# Revit family: Hager-VOLTA-Hollow_wall-IP30-With_Cover-Without_DIN-Hosted-DE-de
name_source: partatom
category: Electrical Equipment
units: mm (PartAtom-declared; Revit-internal decimal feet)

## family parameters
Cut with Voids When Loaded = No
Host = Face
Maintain Annotation Orientation = Yes
Panel Configuration = Two Columns, Circuits Across
Part Type = Panelboard
Room Calculation Point = No
Round Connector Dimension = Use Diameter
Shared = No

## types (6) — shared parameters
BC_MODEL_ID = 1547175
BC_OBJECT_ID = 513479
BC_OBJECT_VERSION = #3
Code hager = ADD-EC000214_EU
EF000003 - Montageart = Hohlwand
EF000007 - Farbe = weiß
EF000008 - Breite = 348 mm  [stored 1.14173 ft]
EF000024 - UV-beständig = No
EF000049 - Tiefe = 98 mm  [stored 0.321522 ft]
EF000116 - RAL-Nummer = 9010
EF000118 - Mit Montageplatte = Yes
EF000218 - Einbautiefe = 89 mm  [stored 0.291995 ft]
EF000846 - Einbaubreite = 315 mm
EF001062 - EMV-Ausführung = No
EF001088 - Anbaumöglichkeit = Yes
EF001134 - DIN-Schiene = No
EF002950 - Breite in Teilungseinheiten = 12
EF004462 - Art der Schließung = sonstige
EF005474 - Schutzart (IP) = IP30
EF006244 - Transparenter Deckel/Tür = No
EF006306 - Mit Schloss = No
EF009212 - Ausführung Deckel = mit Ausschnitt
EF015776 - Erdungsklemmenblock = No
EF015777 - Neutralleiterklemmenblock = No
ETIM class code = EC000214
ETIM class name = Small distribution board
HG000002-Mit tür = Yes
HG000003-Bereich = VOLTA
HG000005-Dicke = 2 mm  [stored 0.00656168 ft]
HG000006-Flush mounted = Yes
HG000009-Doppelflügeligen Tür = No
HG000010-Asymmetrische Türen = No
HG000011-Leere Reihen von unten = No
HG000012-Türschwenkwinkel = 90.00°
HG000013-Tür links = No
HG000014-Tür rechts = Yes
HG000015-Sichtbarkeit der Türöffnung = Yes
HG000016-3D-Türsichtbarkeit = Yes
HG000017-Distanz zwischen den Polen = 18 mm  [stored 0.0590551 ft]
HG000060-RAL-number = 9010
HG000099-Onfly Template ID-de-DE = 507532
HGEF0002950-Breite in Teilungseinheiten = 12
Manufacturer = Hager
Name = VOLTA-Hollow_wall-IP30-With_Cover-Without_DIN-DE
Name BIM&CO = Electricity
Name hager = ADD_Enclosures_EC000214
Uniformat = Low Tension Service & Dist.
Uniformat code = D501001
zero-valued in all types: Default Elevation, EF000266 - Anzahl der Reihen, EF001131 - Innentiefe, HG000001-Anzahl der Spalten, HG000007-Anzahl der leeren Spalten, HG000008-Anzahl der leeren Reihen, HGEF000266-Anzahl der Reihen

## per-type parameters (varying)
| type | BC_VARIANT_ID | EF000040 - Höhe | EF000332 - Einbauhöhe | EF015941 - Signaldurchlassende Tür | HG000004-Herstellerreferenz |
| VOLTA-Hollow_wall_W348_H630_D98_12_Modular_Spacing-VH36NW | 1174185 | 630 mm  [stored 2.06693 ft] | 595 mm  [stored 1.9521 ft] | No | VH36NW |
| VOLTA-Hollow_wall_W348_H630_D98_12_Modular_Spacing-VH36WWH | 1174186 | 630 mm  [stored 2.06693 ft] | 595 mm  [stored 1.9521 ft] | Yes | VH36WWH |
| VOLTA-Hollow_wall_W348_H755_D98_12_Modular_Spacing-VH48NW | 1174187 | 755 mm  [stored 2.47703 ft] | 720 mm  [stored 2.3622 ft] | No | VH48NW |
| VOLTA-Hollow_wall_W348_H755_D98_12_Modular_Spacing-VH48WWH | 1174188 | 755 mm  [stored 2.47703 ft] | 720 mm  [stored 2.3622 ft] | Yes | VH48WWH |
| VOLTA-Hollow_wall_W348_H880_D98_12_Modular_Spacing-VH60NW | 1174189 | 880 mm  [stored 2.88714 ft] | 845 mm  [stored 2.77231 ft] | No | VH60NW |
| VOLTA-Hollow_wall_W348_H880_D98_12_Modular_Spacing-VH60WWH | 1174190 | 880 mm  [stored 2.88714 ft] | 845 mm  [stored 2.77231 ft] | Yes | VH60WWH |

note: column(s) folded — value = type name in every type: Reference

note: [stored X ft] marks values corroborated as IEEE doubles in the binary element streams (Revit-internal decimal feet)

## geometry (parser evidence)
native form markers: Sweep x14
no freeform markers — native parametric forms only
